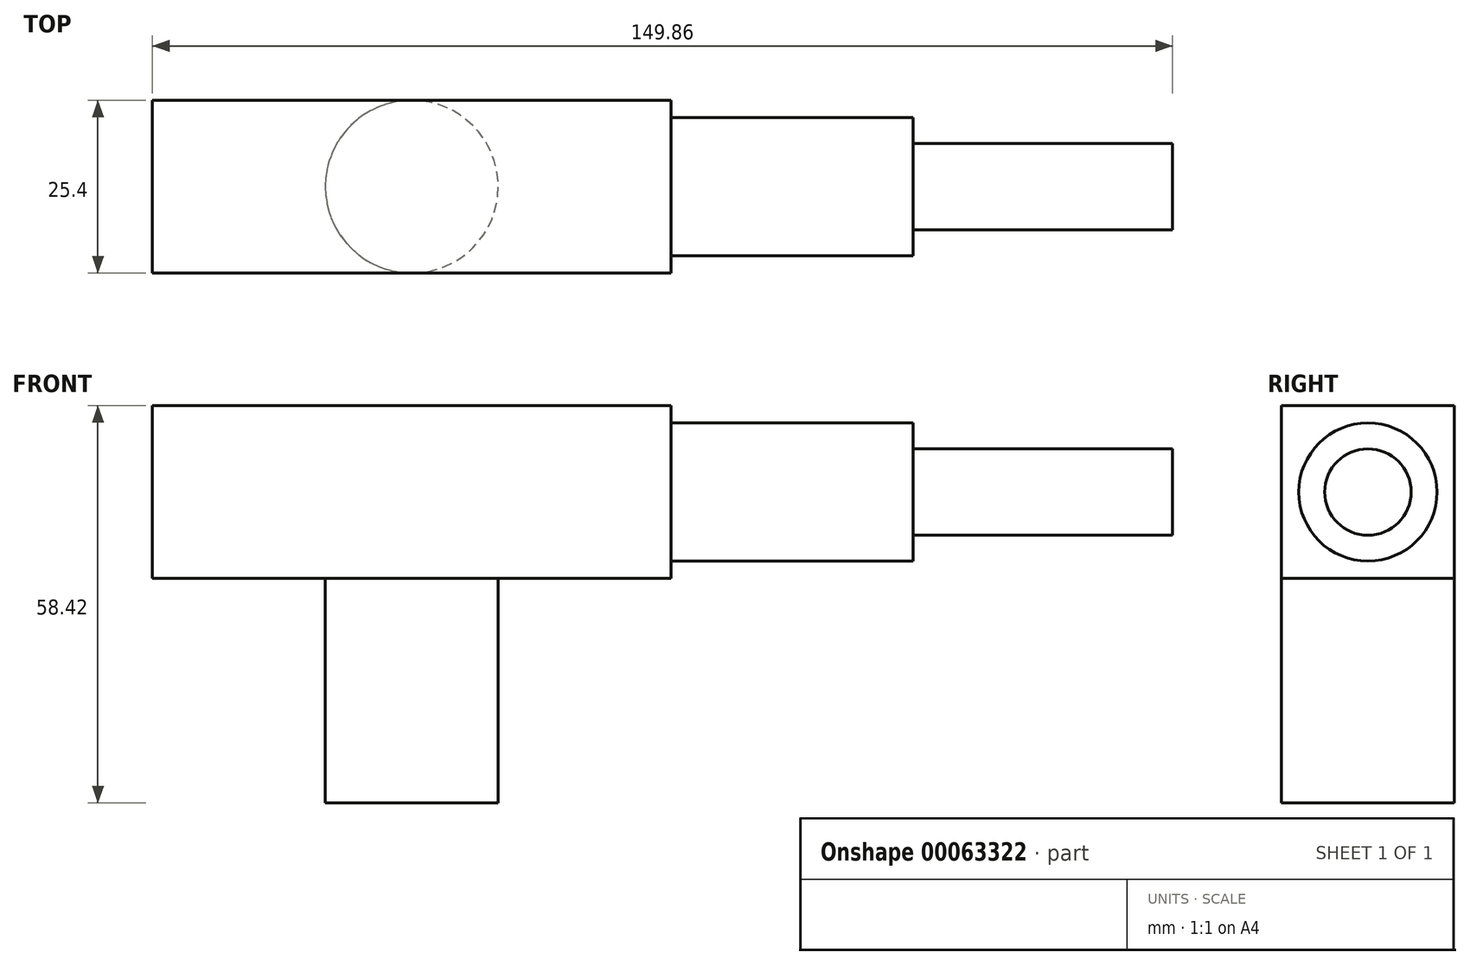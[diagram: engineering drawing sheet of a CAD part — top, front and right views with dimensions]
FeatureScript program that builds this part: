
annotation { "Feature Type Name" : "Feature", "Feature Type Description" : "" }
export const myFeature = defineFeature(function(context is Context, id is Id, definition is map)
    precondition{}
    {
        {
            var Q0;
            Q0=qCreatedBy(makeId("Front.planeOp"),FACE);
            var sketch = newSketch(context, id + "F0", { "sketchPlane" : qUnion([Q0])});
            skLineSegment(sketch, "E0.rect.bottom", {"start": v(38.1, 12.7) * mm, "end": v(-38.1, 12.7) * mm});
            skLineSegment(sketch, "E0.rect.top", {"start": v(38.1, -12.7) * mm, "end": v(-38.1, -12.7) * mm});
            skLineSegment(sketch, "E0.rect.left", {"start": v(38.1, 12.7) * mm, "end": v(38.1, -12.7) * mm});
            skLineSegment(sketch, "E0.rect.right", {"start": v(-38.1, 12.7) * mm, "end": v(-38.1, -12.7) * mm});
            skPoint(sketch, "E0.rect.middle", {"position": v(0, 0) * mm});
            skSolve(sketch);
        }
        {
            var Q0;
            Q0=makeQuery(id+"F0.imprint","IMPRINT",FACE,{"disambiguationData":[TD([[makeQuery(id+"F0.imprint","IMPRINT",EDGE,{"derivedFrom":sQuery(id+"F0.wireOp",EDGE,"E0.rect.bottom")}),1.0]])]});
            extrude(context, id + "F1", {"entities" : qUnion([Q0]), "endBound" : BoundingType.SYMMETRIC, "depth" : 25.4 * mm});
        }
        {
            var Q0;
            Q0=makeQuery(id+"F1.opExtrude","SWEPT_FACE",FACE,{"disambiguationData":[OSD([sQuery(id+"F0.wireOp",EDGE,"E0.rect.top")])]});
            var sketch = newSketch(context, id + "F2", { "sketchPlane" : qUnion([Q0])});
            skCircle(sketch, "E1", {"center": v(0, 0) * mm, "radius": 12.7 * mm});
            skSolve(sketch);
        }
        {
            var Q0;
            {var subQ0=sQuery(id+"F2.wireOp",EDGE,"E1");var subQ1=sQuery(id+"F0.wireOp",EDGE,"E0.rect.top");var subQ2=makeQuery(id+"F2.imprint","INTERSECT",VERTEX,{"derivedFrom":[makeQuery(id+"F1.opExtrude","CAP_EDGE",EDGE,{"disambiguationData":[OSD([subQ1])],"isStart":true}),subQ0]});Q0=makeQuery(id+"F2.imprint","IMPRINT",FACE,{"disambiguationData":[TD([[makeQuery(id+"F2.imprint","IMPRINT",EDGE,{"disambiguationData":[TD([[subQ2,1.0]])],"derivedFrom":subQ0}),1.0]])]});}
            extrude(context, id + "F3", {"entities" : qUnion([Q0]), "operationType" : NewBodyOperationType.ADD, "depth" : 33.02 * mm});
        }
        {
            var Q0;
            Q0=makeQuery(id+"F1.opExtrude","SWEPT_FACE",FACE,{"disambiguationData":[OSD([sQuery(id+"F0.wireOp",EDGE,"E0.rect.left")])]});
            var sketch = newSketch(context, id + "F4", { "sketchPlane" : qUnion([Q0])});
            skCircle(sketch, "E2", {"center": v(0, 0) * mm, "radius": 10.16 * mm});
            skSolve(sketch);
        }
        {
            var Q0;
            Q0=makeQuery(id+"F4.imprint","IMPRINT",FACE,{"disambiguationData":[TD([[makeQuery(id+"F4.imprint","IMPRINT",EDGE,{"derivedFrom":sQuery(id+"F4.wireOp",EDGE,"E2")}),1.0]])]});
            extrude(context, id + "F5", {"entities" : qUnion([Q0]), "operationType" : NewBodyOperationType.ADD, "depth" : 35.56 * mm});
        }
        {
            var Q0;
            Q0=makeQuery(id+"F5.opExtrude","CAP_FACE",FACE,{"disambiguationData":[OSD([sQuery(id+"F4.wireOp",EDGE,"E2")])],"isStart":false});
            var sketch = newSketch(context, id + "F6", { "sketchPlane" : qUnion([Q0])});
            skCircle(sketch, "E3", {"center": v(0, 0) * mm, "radius": 6.35 * mm});
            skSolve(sketch);
        }
        {
            var Q0;
            Q0=makeQuery(id+"F6.imprint","IMPRINT",FACE,{"disambiguationData":[TD([[makeQuery(id+"F6.imprint","IMPRINT",EDGE,{"derivedFrom":sQuery(id+"F6.wireOp",EDGE,"E3")}),1.0]])]});
            extrude(context, id + "F7", {"entities" : qUnion([Q0]), "operationType" : NewBodyOperationType.ADD, "depth" : 38.1 * mm});
        }
    });
